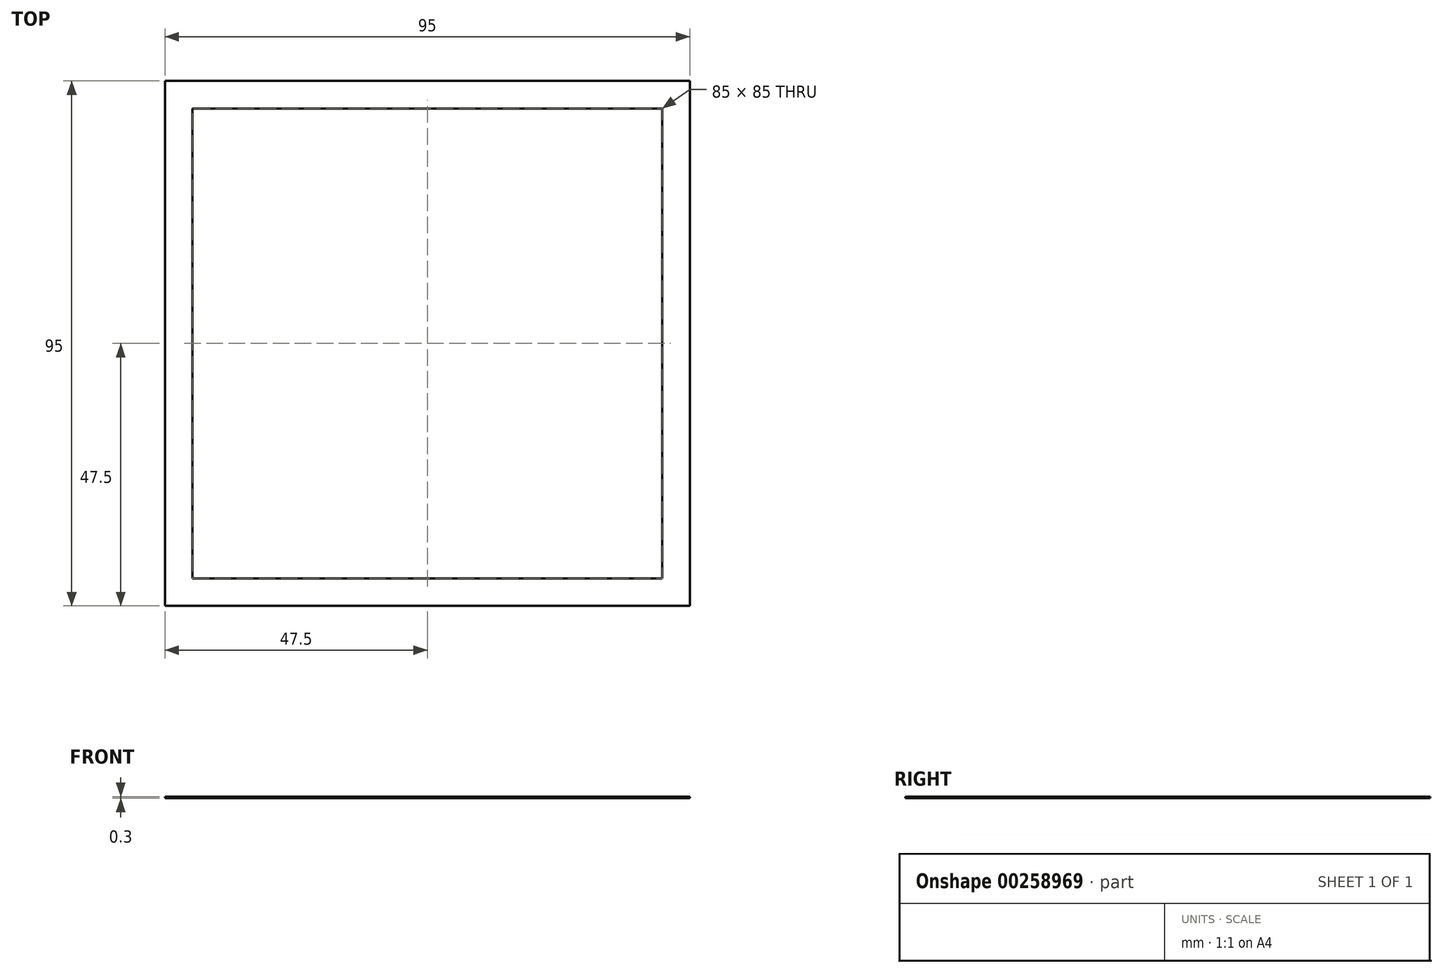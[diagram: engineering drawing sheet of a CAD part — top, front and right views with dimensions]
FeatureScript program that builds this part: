
annotation { "Feature Type Name" : "Feature", "Feature Type Description" : "" }
export const myFeature = defineFeature(function(context is Context, id is Id, definition is map)
    precondition{}
    {
        {
            var Q0;
            Q0=qCreatedBy(makeId("Top.planeOp"),FACE);
            var sketch = newSketch(context, id + "F0", { "sketchPlane" : qUnion([Q0])});
            skLineSegment(sketch, "E0.bottom", {"start": v(0, 0) * mm, "end": v(95, 0) * mm});
            skLineSegment(sketch, "E0.top", {"start": v(0, 95) * mm, "end": v(95, 95) * mm});
            skLineSegment(sketch, "E0.left", {"start": v(0, 0) * mm, "end": v(0, 95) * mm});
            skLineSegment(sketch, "E0.right", {"start": v(95, 0) * mm, "end": v(95, 95) * mm});
            skLineSegment(sketch, "E1.0", {"start": v(5, 90) * mm, "end": v(90, 90) * mm});
            skLineSegment(sketch, "E1.1", {"start": v(5, 5) * mm, "end": v(5, 90) * mm});
            skLineSegment(sketch, "E1.2", {"start": v(5, 5) * mm, "end": v(90, 5) * mm});
            skLineSegment(sketch, "E1.3", {"start": v(90, 5) * mm, "end": v(90, 90) * mm});
            skSolve(sketch);
        }
        {
            var Q0;
            Q0 = qSketchRegion(id + "F0", true);
            extrude(context, id + "F1", {"entities" : qUnion([Q0]), "depth" : .3 * mm});
        }
    });
